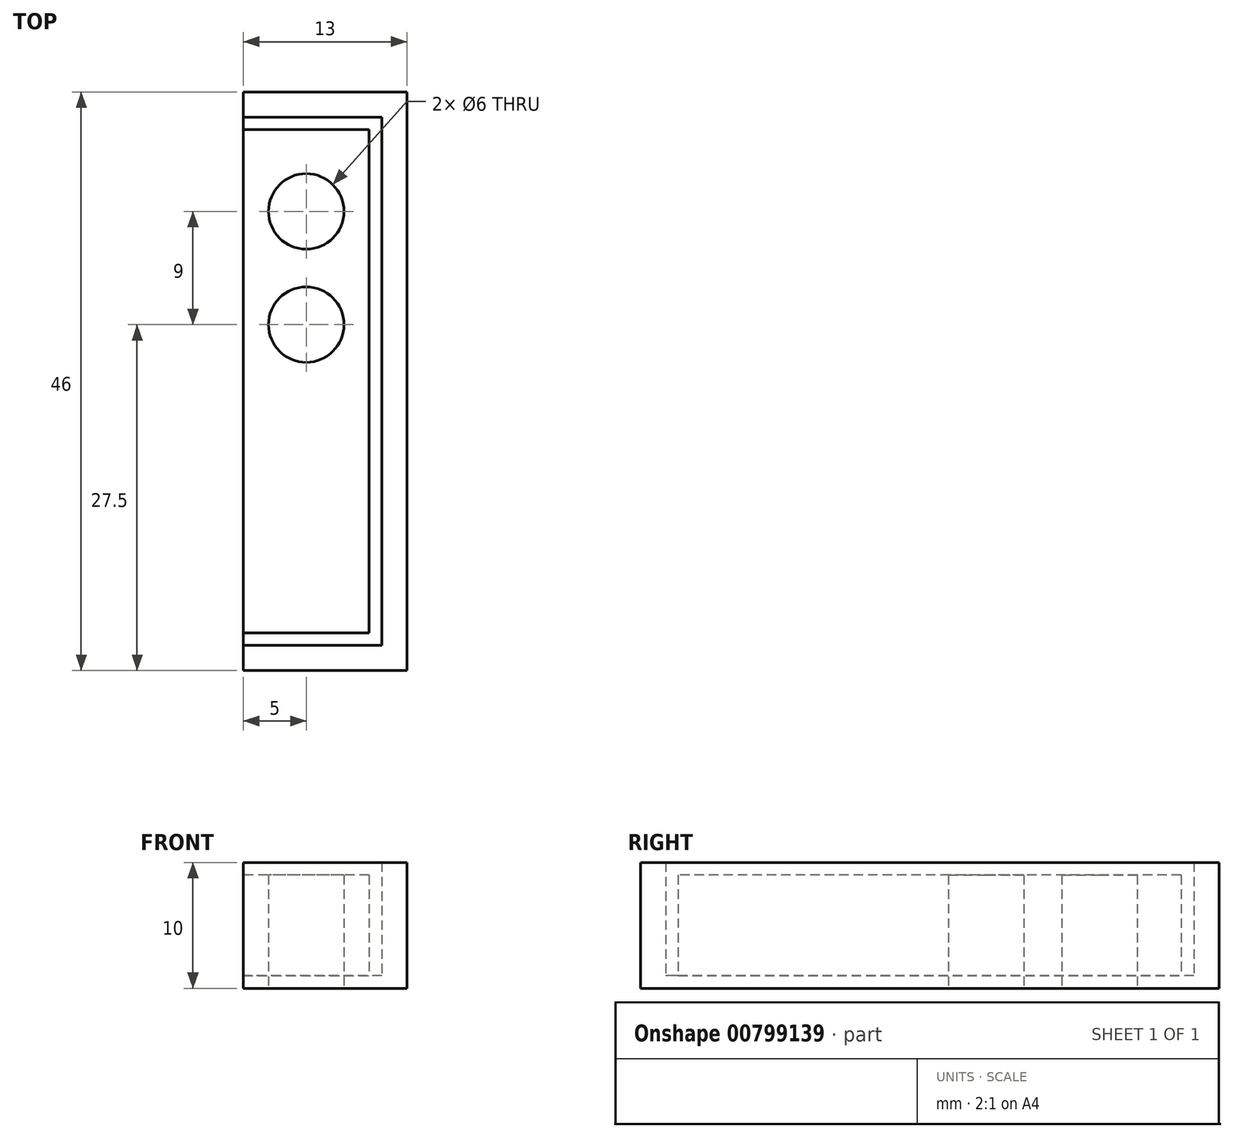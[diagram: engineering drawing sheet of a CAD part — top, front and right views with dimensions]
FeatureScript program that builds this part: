
annotation { "Feature Type Name" : "Feature", "Feature Type Description" : "" }
export const myFeature = defineFeature(function(context is Context, id is Id, definition is map)
    precondition{}
    {
        {
            var Q0;
            Q0=qCreatedBy(makeId("Top.planeOp"),FACE);
            var sketch = newSketch(context, id + "F0", { "sketchPlane" : qUnion([Q0])});
            skLineSegment(sketch, "E0.bottom", {"start": v(5, 20) * mm, "end": v(-5, 20) * mm});
            skLineSegment(sketch, "E0.top", {"start": v(5, -20) * mm, "end": v(-5, -20) * mm});
            skLineSegment(sketch, "E0.left", {"start": v(5, 20) * mm, "end": v(5, -20) * mm});
            skLineSegment(sketch, "E0.right", {"start": v(-5, 20) * mm, "end": v(-5, -20) * mm});
            skPoint(sketch, "E0.middle", {"position": v(0, 0) * mm});
            skLineSegment(sketch, "E1", {"start": v(0, -20) * mm, "end": v(0, -13.5) * mm});
            skCircle(sketch, "E2", {"center": v(0, -13.5) * mm, "radius": 3 * mm});
            skLineSegment(sketch, "E3", {"start": v(0, -13.5) * mm, "end": v(0, -4.5) * mm});
            skCircle(sketch, "E4", {"center": v(0, -4.5) * mm, "radius": 3 * mm});
            skCircle(sketch, "E5.MirrorC", {"center": v(0, 4.5) * mm, "radius": 3 * mm});
            skCircle(sketch, "E6.MirrorC", {"center": v(0, 13.5) * mm, "radius": 3 * mm});
            skLineSegment(sketch, "E7.0", {"start": v(8, 23) * mm, "end": v(-5, 23) * mm});
            skLineSegment(sketch, "E7.1", {"start": v(8, 23) * mm, "end": v(8, -23) * mm});
            skLineSegment(sketch, "E7.2", {"start": v(8, -23) * mm, "end": v(-5, -23) * mm});
            skLineSegment(sketch, "E8.0", {"start": v(6, 21) * mm, "end": v(-5, 21) * mm});
            skLineSegment(sketch, "E8.1", {"start": v(6, 21) * mm, "end": v(6, -21) * mm});
            skLineSegment(sketch, "E8.2", {"start": v(6, -21) * mm, "end": v(-5, -21) * mm});
            skLineSegment(sketch, "E9", {"start": v(-5, 23) * mm, "end": v(-5, 21) * mm});
            skLineSegment(sketch, "E10", {"start": v(-5, 20) * mm, "end": v(-5, 21) * mm});
            skLineSegment(sketch, "E11", {"start": v(-5, -20) * mm, "end": v(-5, -21) * mm});
            skLineSegment(sketch, "E12", {"start": v(-5, -21) * mm, "end": v(-5, -23) * mm});
            skSolve(sketch);
        }
        {
            var Q0;
            Q0=makeQuery(id+"F0.imprint","IMPRINT",FACE,{"disambiguationData":[TD([[makeQuery(id+"F0.imprint","IMPRINT",EDGE,{"derivedFrom":sQuery(id+"F0.wireOp",EDGE,"E0.bottom")}),1.0]])]});
            var Q1;
            Q1=makeQuery(id+"F0.imprint","IMPRINT",FACE,{"disambiguationData":[TD([[makeQuery(id+"F0.imprint","IMPRINT",EDGE,{"derivedFrom":sQuery(id+"F0.wireOp",EDGE,"E0.bottom")}),-1.0]])]});
            extrude(context, id + "F1", {"entities" : qUnion([Q0, Q1]), "depth" : 1 * mm, "offsetDistance" : 25 * mm});
        }
        {
            var Q0;
            Q0=makeQuery(id+"F0.imprint","IMPRINT",FACE,{"disambiguationData":[TD([[makeQuery(id+"F0.imprint","IMPRINT",EDGE,{"derivedFrom":sQuery(id+"F0.wireOp",EDGE,"E7.0")}),1.0]])]});
            extrude(context, id + "F2", {"entities" : qUnion([Q0]), "operationType" : NewBodyOperationType.ADD, "depth" : 10 * mm, "offsetDistance" : 25 * mm});
        }
        {
            var Q0;
            Q0=makeQuery(id+"F0.imprint","IMPRINT",FACE,{"disambiguationData":[TD([[makeQuery(id+"F0.imprint","IMPRINT",EDGE,{"derivedFrom":sQuery(id+"F0.wireOp",EDGE,"E6.MirrorC")}),-1.0]])]});
            var Q1;
            Q1=makeQuery(id+"F0.imprint","IMPRINT",FACE,{"disambiguationData":[TD([[makeQuery(id+"F0.imprint","IMPRINT",EDGE,{"derivedFrom":sQuery(id+"F0.wireOp",EDGE,"E5.MirrorC")}),-1.0]])]});
            var Q2;
            Q2=makeQuery(id+"F0.imprint","IMPRINT",FACE,{"disambiguationData":[TD([[makeQuery(id+"F0.imprint","IMPRINT",EDGE,{"derivedFrom":sQuery(id+"F0.wireOp",EDGE,"E4")}),1.0]])]});
            var Q3;
            {var subQ0=sQuery(id+"F0.wireOp",EDGE,"E3");var subQ1=sQuery(id+"F0.wireOp",EDGE,"E1");var subQ2=makeQuery(id+"F0.imprint","INTERSECT",VERTEX,{"derivedFrom":[subQ1,subQ0]});Q3=makeQuery(id+"F0.imprint","IMPRINT",FACE,{"disambiguationData":[TD([[makeQuery(id+"F0.imprint","IMPRINT",EDGE,{"disambiguationData":[TD([[subQ2,1.0]])],"derivedFrom":subQ1}),-1.0]])]});}
            var Q4;
            {var subQ0=sQuery(id+"F0.wireOp",EDGE,"E3");var subQ1=sQuery(id+"F0.wireOp",EDGE,"E1");var subQ2=makeQuery(id+"F0.imprint","INTERSECT",VERTEX,{"derivedFrom":[subQ1,subQ0]});Q4=makeQuery(id+"F0.imprint","IMPRINT",FACE,{"disambiguationData":[TD([[makeQuery(id+"F0.imprint","IMPRINT",EDGE,{"disambiguationData":[TD([[subQ2,1.0]])],"derivedFrom":subQ1}),1.0]])]});}
            extrude(context, id + "F3", {"entities" : qUnion([Q0, Q1, Q2, Q3, Q4]), "operationType" : NewBodyOperationType.ADD, "depth" : 9 * mm, "offsetDistance" : 25 * mm});
        }
    });
